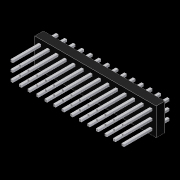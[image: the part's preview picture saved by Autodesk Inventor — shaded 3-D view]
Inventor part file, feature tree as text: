
AUTODESK INVENTOR PART (.ipt)
format: ipt  version: 2012 (Build 160160000, 160)  size: 307,200 bytes
history: native  units: in
note: dims shown in document units (in); Inventor stores cm internally (conversion verified against a paired STEP export)
features: extrude x3, sketch x1, pattern_linear x1
ambient origin geometry x8: Origin, YZ Plane, XZ Plane, XY Plane, X Axis, Y Axis, Z Axis, Center Point
bodies: Solid1 (feature_tree)
feature tree (5):
  sketch  "Sketch1"  dims[d0=0.0in d1=0.025in d2=0.025in d3=0.025in d4=0.025in d6=0.0475in d7=0.0475in d8=0.1in d9=0.0in d10=0.33in d11=0.0in d12=5.5118in d14=0.1in d15=1.1811in d17=0.1in d18=0.2in d19=0.0in]
  extrude  "Extrusion1"  Depth=0.025in
  extrude  "Extrusion2"  Depth=0.025in
  extrude  "Extrusion3"  Depth=0.025in
  pattern_linear  "Rectangular Pattern1"  Spacing1=0.025in  [1 undecoded]
note: 1 required parameter value undecoded (feature->parameter linkage not recoverable at this tier; creation-order binding heuristic only, values carry confidence <= 0.55)
